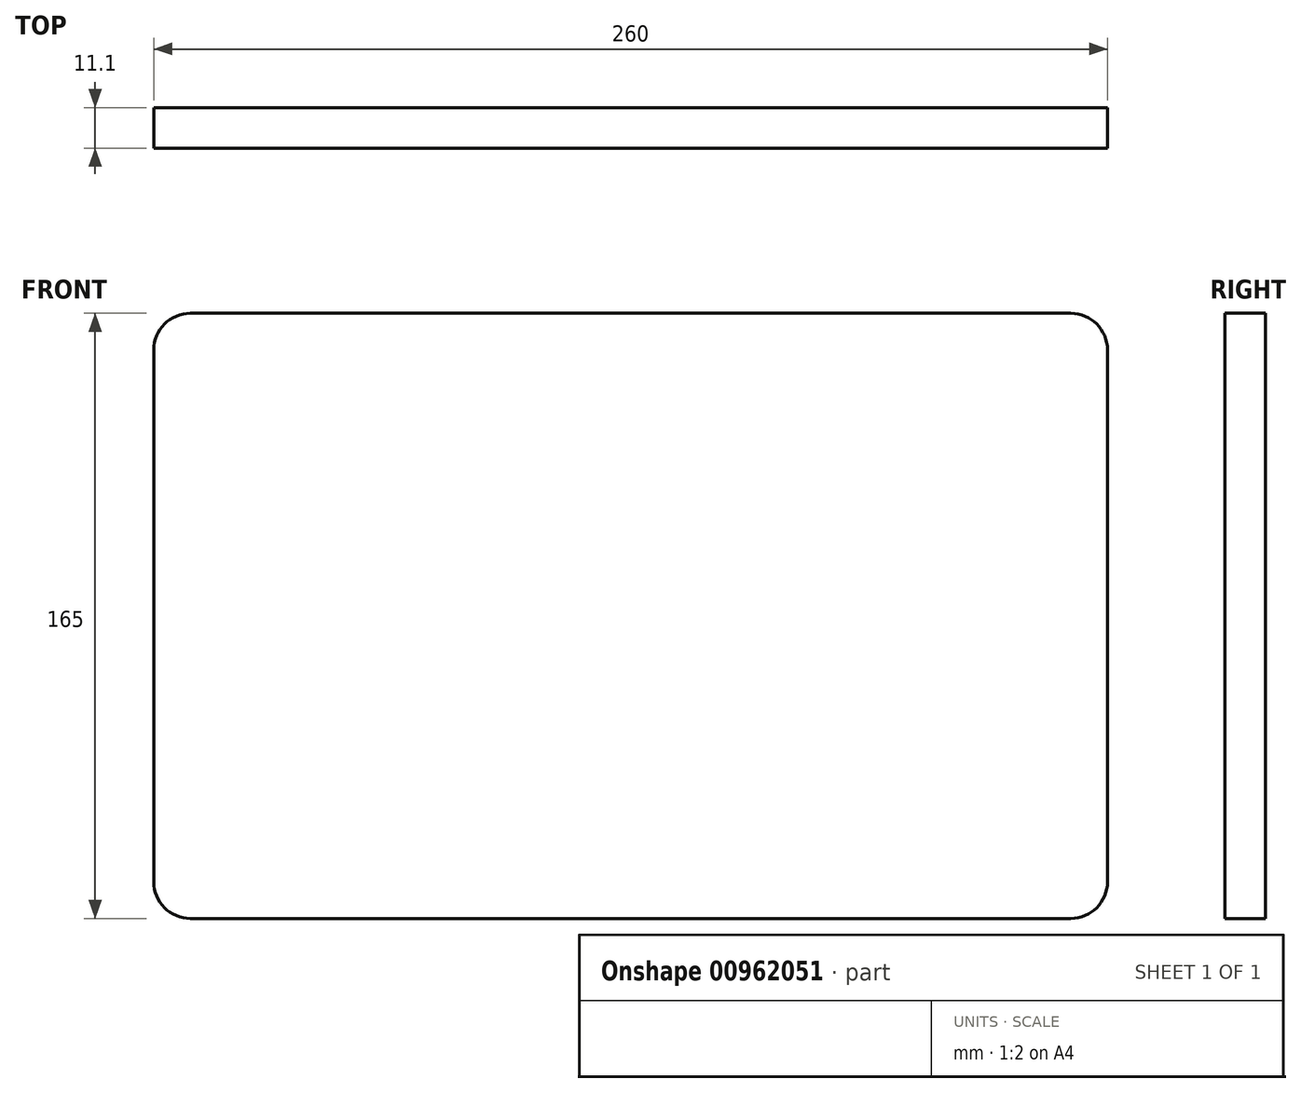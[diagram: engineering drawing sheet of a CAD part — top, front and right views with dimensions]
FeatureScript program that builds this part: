
annotation { "Feature Type Name" : "Feature", "Feature Type Description" : "" }
export const myFeature = defineFeature(function(context is Context, id is Id, definition is map)
    precondition{}
    {
        {
            var Q0;
            Q0=qCreatedBy(makeId("Front.planeOp"),FACE);
            var sketch = newSketch(context, id + "F0", { "sketchPlane" : qUnion([Q0])});
            skLineSegment(sketch, "E0.bottom", {"start": v(130, -82.5) * mm, "end": v(-130, -82.5) * mm});
            skLineSegment(sketch, "E0.top", {"start": v(130, 82.5) * mm, "end": v(-130, 82.5) * mm});
            skLineSegment(sketch, "E0.left", {"start": v(130, -82.5) * mm, "end": v(130, 82.5) * mm});
            skLineSegment(sketch, "E0.right", {"start": v(-130, -82.5) * mm, "end": v(-130, 82.5) * mm});
            skPoint(sketch, "E0.middle", {"position": v(0, 0) * mm});
            skSolve(sketch);
        }
        {
            var Q0;
            Q0 = qSketchRegion(id + "F0", true);
            extrude(context, id + "F1", {"entities" : qUnion([Q0]), "depth" : 11.1 * mm, "offsetDistance" : 25.4 * mm});
        }
        {
            var Q0;
            Q0=makeQuery(id+"F1.opExtrude","SWEPT_EDGE",EDGE,{"disambiguationData":[OSD([sQuery(id+"F0.wireOp",EDGE,"E0.bottom"),sQuery(id+"F0.wireOp",EDGE,"E0.right")])]});
            var Q1;
            Q1=makeQuery(id+"F1.opExtrude","SWEPT_EDGE",EDGE,{"disambiguationData":[OSD([sQuery(id+"F0.wireOp",EDGE,"E0.bottom"),sQuery(id+"F0.wireOp",EDGE,"E0.left")])]});
            var Q2;
            Q2=makeQuery(id+"F1.opExtrude","SWEPT_EDGE",EDGE,{"disambiguationData":[OSD([sQuery(id+"F0.wireOp",EDGE,"E0.top"),sQuery(id+"F0.wireOp",EDGE,"E0.left")])]});
            var Q3;
            Q3=makeQuery(id+"F1.opExtrude","SWEPT_EDGE",EDGE,{"disambiguationData":[OSD([sQuery(id+"F0.wireOp",EDGE,"E0.top"),sQuery(id+"F0.wireOp",EDGE,"E0.right")])]});
            fillet(context, id + "F2", {"entities" : qUnion([Q0, Q1, Q2, Q3]), "radius" : 10 * mm, "tangentPropagation" : true, "allowEdgeOverflow" : false});
        }
    });
